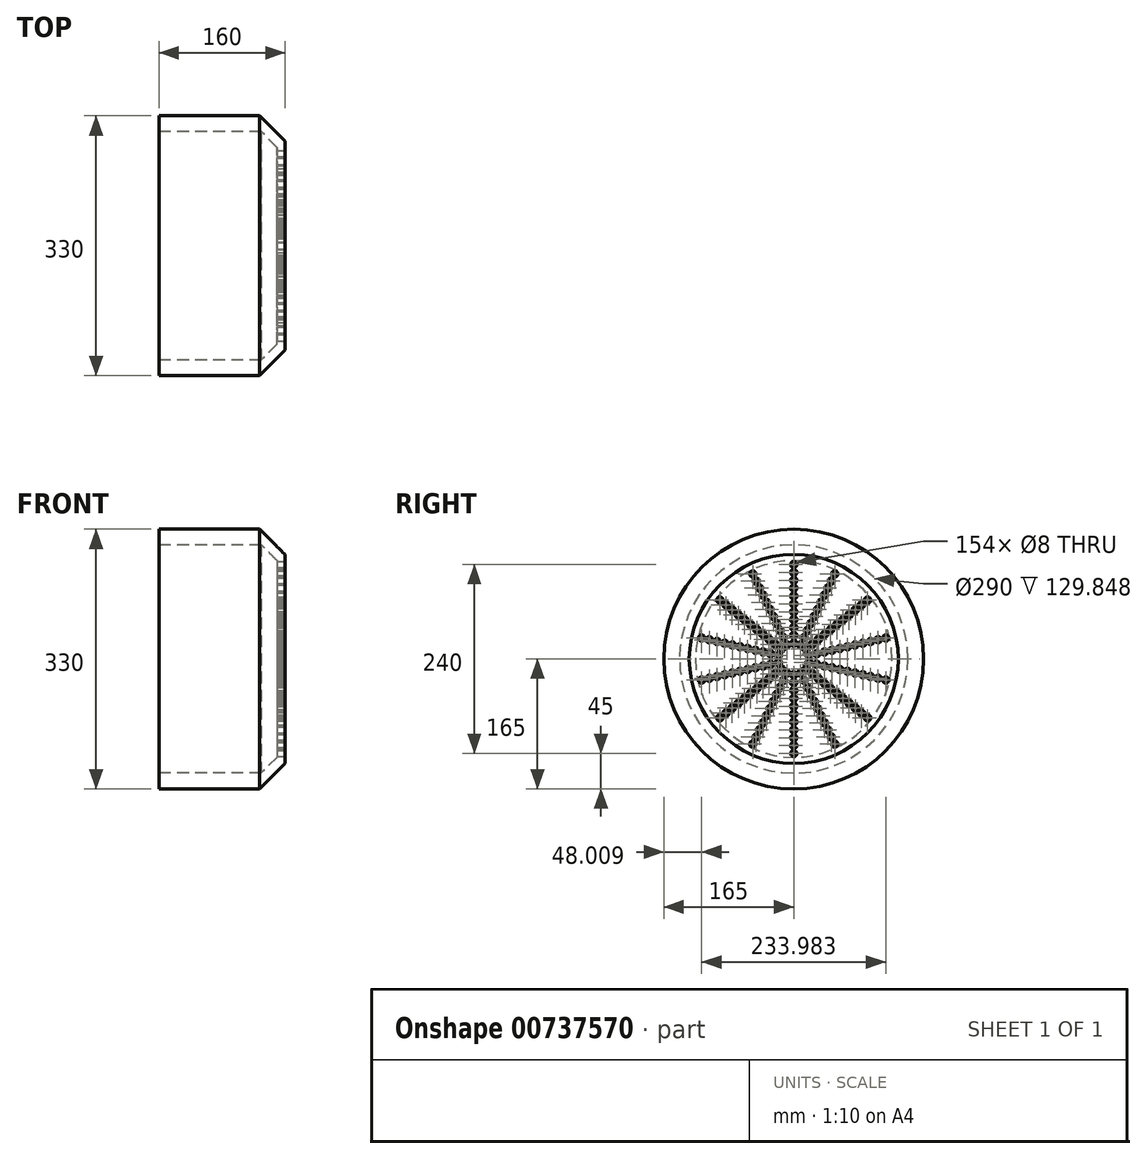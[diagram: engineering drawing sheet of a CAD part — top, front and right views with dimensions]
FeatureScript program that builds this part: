
annotation { "Feature Type Name" : "Feature", "Feature Type Description" : "" }
export const myFeature = defineFeature(function(context is Context, id is Id, definition is map)
    precondition{}
    {
        {
            var Q0;
            Q0=qCreatedBy(makeId("Front.planeOp"),FACE);
            var sketch = newSketch(context, id + "F0", { "sketchPlane" : qUnion([Q0])});
            skLineSegment(sketch, "E0.bottom", {"start": v(170, 0) * mm, "end": v(180, 0) * mm});
            skLineSegment(sketch, "E0.top", {"start": v(20, 165) * mm, "end": v(147.78, 165) * mm});
            skLineSegment(sketch, "E0.left", {"start": v(20, 145) * mm, "end": v(20, 165) * mm});
            skLineSegment(sketch, "E0.right", {"start": v(180, 0) * mm, "end": v(180, 132.78) * mm});
            skLineSegment(sketch, "E1", {"start": v(20, 145) * mm, "end": v(125.56, 145) * mm});
            skLineSegment(sketch, "E2", {"start": v(170, 100.56) * mm, "end": v(170, 0) * mm});
            skLineSegment(sketch, "E3", {"start": v(147.78, 165) * mm, "end": v(180, 132.78) * mm});
            skPoint(sketch, "E3.startSnap0", {"position": v(147.78, 122.78) * mm});
            skLineSegment(sketch, "E4", {"start": v(170, 100.56) * mm, "end": v(170, 124.85) * mm});
            skLineSegment(sketch, "E5", {"start": v(170, 124.85) * mm, "end": v(149.85, 145) * mm});
            skLineSegment(sketch, "E6", {"start": v(125.56, 145) * mm, "end": v(149.85, 145) * mm});
            skSolve(sketch);
        }
        {
            var Q0;
            Q0 = qSketchRegion(id + "F0", true);
            var Q1;
            Q1=sQuery(id+"F0.wireOp",EDGE,"E0.bottom");
            revolve(context, id + "F1", {"surfaceOperationType" : NewSurfaceOperationType.NEW, "entities" : qUnion([Q0]), "axis" : qUnion([Q1]), "revolveType" : RevolveType.FULL});
        }
        {
            var Q0;
            Q0=makeQuery(id+"F1.opRevolve","SWEPT_FACE",FACE,{"disambiguationData":[OSD([sQuery(id+"F0.wireOp",EDGE,"E0.right")])]});
            var sketch = newSketch(context, id + "F2", { "sketchPlane" : qUnion([Q0])});
            skCircle(sketch, "E7", {"center": v(0, 20) * mm, "radius": 4 * mm});
            skCircle(sketch, "E8.0.1.0", {"center": v(0, 30) * mm, "radius": 4 * mm});
            skCircle(sketch, "E8.0.2.0", {"center": v(0, 40) * mm, "radius": 4 * mm});
            skCircle(sketch, "E8.0.3.0", {"center": v(0, 50) * mm, "radius": 4 * mm});
            skCircle(sketch, "E8.0.4.0", {"center": v(0, 60) * mm, "radius": 4 * mm});
            skCircle(sketch, "E8.0.5.0", {"center": v(0, 70) * mm, "radius": 4 * mm});
            skCircle(sketch, "E8.0.6.0", {"center": v(0, 80) * mm, "radius": 4 * mm});
            skCircle(sketch, "E8.0.7.0", {"center": v(0, 90) * mm, "radius": 4 * mm});
            skCircle(sketch, "E8.0.8.0", {"center": v(0, 100) * mm, "radius": 4 * mm});
            skCircle(sketch, "E8.0.9.0", {"center": v(0, 110) * mm, "radius": 4 * mm});
            skCircle(sketch, "E8.0.10.0", {"center": v(0, 120) * mm, "radius": 4 * mm});
            skLineSegment(sketch, "E8.direction1", {"start": v(0, 20) * mm, "end": v(25, 20) * mm, "construction": true});
            skLineSegment(sketch, "E8.direction2", {"start": v(0, 20) * mm, "end": v(0, 30) * mm, "construction": true});
            skCircle(sketch, "E9.1.0", {"center": v(-21.7, 45.05) * mm, "radius": 4 * mm});
            skCircle(sketch, "E9.1.1", {"center": v(-13.02, 27.03) * mm, "radius": 4 * mm});
            skCircle(sketch, "E9.1.2", {"center": v(-43.39, 90.1) * mm, "radius": 4 * mm});
            skCircle(sketch, "E9.1.3", {"center": v(-39.05, 81.09) * mm, "radius": 4 * mm});
            skCircle(sketch, "E9.1.4", {"center": v(-26.03, 54.06) * mm, "radius": 4 * mm});
            skCircle(sketch, "E9.1.5", {"center": v(-30.37, 63.07) * mm, "radius": 4 * mm});
            skCircle(sketch, "E9.1.6", {"center": v(-34.71, 72.08) * mm, "radius": 4 * mm});
            skCircle(sketch, "E9.1.7", {"center": v(-8.68, 18.02) * mm, "radius": 4 * mm});
            skCircle(sketch, "E9.1.8", {"center": v(-17.36, 36.04) * mm, "radius": 4 * mm});
            skCircle(sketch, "E9.1.9", {"center": v(-52.07, 108.12) * mm, "radius": 4 * mm});
            skCircle(sketch, "E9.1.10", {"center": v(-47.73, 99.1) * mm, "radius": 4 * mm});
            skLineSegment(sketch, "E9.1.11", {"start": v(-8.68, 18.02) * mm, "end": v(-13.02, 27.03) * mm, "construction": true});
            skCircle(sketch, "E9.2.0", {"center": v(-39.1, 31.17) * mm, "radius": 4 * mm});
            skCircle(sketch, "E9.2.1", {"center": v(-23.45, 18.7) * mm, "radius": 4 * mm});
            skCircle(sketch, "E9.2.2", {"center": v(-78.18, 62.35) * mm, "radius": 4 * mm});
            skCircle(sketch, "E9.2.3", {"center": v(-70.36, 56.11) * mm, "radius": 4 * mm});
            skCircle(sketch, "E9.2.4", {"center": v(-46.9, 37.4) * mm, "radius": 4 * mm});
            skCircle(sketch, "E9.2.5", {"center": v(-54.73, 43.64) * mm, "radius": 4 * mm});
            skCircle(sketch, "E9.2.6", {"center": v(-62.55, 49.88) * mm, "radius": 4 * mm});
            skCircle(sketch, "E9.2.7", {"center": v(-15.64, 12.47) * mm, "radius": 4 * mm});
            skCircle(sketch, "E9.2.8", {"center": v(-31.27, 24.94) * mm, "radius": 4 * mm});
            skCircle(sketch, "E9.2.9", {"center": v(-93.82, 74.82) * mm, "radius": 4 * mm});
            skCircle(sketch, "E9.2.10", {"center": v(-86, 68.58) * mm, "radius": 4 * mm});
            skLineSegment(sketch, "E9.2.11", {"start": v(-15.64, 12.47) * mm, "end": v(-23.45, 18.7) * mm, "construction": true});
            skCircle(sketch, "E9.3.0", {"center": v(-48.75, 11.13) * mm, "radius": 4 * mm});
            skCircle(sketch, "E9.3.1", {"center": v(-29.25, 6.68) * mm, "radius": 4 * mm});
            skCircle(sketch, "E9.3.2", {"center": v(-97.5, 22.25) * mm, "radius": 4 * mm});
            skCircle(sketch, "E9.3.3", {"center": v(-87.74, 20.03) * mm, "radius": 4 * mm});
            skCircle(sketch, "E9.3.4", {"center": v(-58.5, 13.35) * mm, "radius": 4 * mm});
            skCircle(sketch, "E9.3.5", {"center": v(-68.24, 15.58) * mm, "radius": 4 * mm});
            skCircle(sketch, "E9.3.6", {"center": v(-78, 17.8) * mm, "radius": 4 * mm});
            skCircle(sketch, "E9.3.7", {"center": v(-19.5, 4.45) * mm, "radius": 4 * mm});
            skCircle(sketch, "E9.3.8", {"center": v(-39, 8.9) * mm, "radius": 4 * mm});
            skCircle(sketch, "E9.3.9", {"center": v(-117, 26.7) * mm, "radius": 4 * mm});
            skCircle(sketch, "E9.3.10", {"center": v(-107.24, 24.48) * mm, "radius": 4 * mm});
            skLineSegment(sketch, "E9.3.11", {"start": v(-19.5, 4.45) * mm, "end": v(-29.25, 6.68) * mm, "construction": true});
            skCircle(sketch, "E9.4.0", {"center": v(-48.75, -11.13) * mm, "radius": 4 * mm});
            skCircle(sketch, "E9.4.1", {"center": v(-29.25, -6.68) * mm, "radius": 4 * mm});
            skCircle(sketch, "E9.4.2", {"center": v(-97.5, -22.25) * mm, "radius": 4 * mm});
            skCircle(sketch, "E9.4.3", {"center": v(-87.74, -20.03) * mm, "radius": 4 * mm});
            skCircle(sketch, "E9.4.4", {"center": v(-58.5, -13.35) * mm, "radius": 4 * mm});
            skCircle(sketch, "E9.4.5", {"center": v(-68.24, -15.58) * mm, "radius": 4 * mm});
            skCircle(sketch, "E9.4.6", {"center": v(-78, -17.8) * mm, "radius": 4 * mm});
            skCircle(sketch, "E9.4.7", {"center": v(-19.5, -4.45) * mm, "radius": 4 * mm});
            skCircle(sketch, "E9.4.8", {"center": v(-39, -8.9) * mm, "radius": 4 * mm});
            skCircle(sketch, "E9.4.9", {"center": v(-117, -26.7) * mm, "radius": 4 * mm});
            skCircle(sketch, "E9.4.10", {"center": v(-107.24, -24.48) * mm, "radius": 4 * mm});
            skLineSegment(sketch, "E9.4.11", {"start": v(-19.5, -4.45) * mm, "end": v(-29.25, -6.68) * mm, "construction": true});
            skCircle(sketch, "E9.5.0", {"center": v(-39.1, -31.17) * mm, "radius": 4 * mm});
            skCircle(sketch, "E9.5.1", {"center": v(-23.45, -18.7) * mm, "radius": 4 * mm});
            skCircle(sketch, "E9.5.2", {"center": v(-78.18, -62.35) * mm, "radius": 4 * mm});
            skCircle(sketch, "E9.5.3", {"center": v(-70.36, -56.11) * mm, "radius": 4 * mm});
            skCircle(sketch, "E9.5.4", {"center": v(-46.9, -37.4) * mm, "radius": 4 * mm});
            skCircle(sketch, "E9.5.5", {"center": v(-54.73, -43.64) * mm, "radius": 4 * mm});
            skCircle(sketch, "E9.5.6", {"center": v(-62.55, -49.88) * mm, "radius": 4 * mm});
            skCircle(sketch, "E9.5.7", {"center": v(-15.64, -12.47) * mm, "radius": 4 * mm});
            skCircle(sketch, "E9.5.8", {"center": v(-31.27, -24.94) * mm, "radius": 4 * mm});
            skCircle(sketch, "E9.5.9", {"center": v(-93.82, -74.82) * mm, "radius": 4 * mm});
            skCircle(sketch, "E9.5.10", {"center": v(-86, -68.58) * mm, "radius": 4 * mm});
            skLineSegment(sketch, "E9.5.11", {"start": v(-15.64, -12.47) * mm, "end": v(-23.45, -18.7) * mm, "construction": true});
            skCircle(sketch, "E9.6.0", {"center": v(-21.7, -45.05) * mm, "radius": 4 * mm});
            skCircle(sketch, "E9.6.1", {"center": v(-13.02, -27.03) * mm, "radius": 4 * mm});
            skCircle(sketch, "E9.6.2", {"center": v(-43.39, -90.1) * mm, "radius": 4 * mm});
            skCircle(sketch, "E9.6.3", {"center": v(-39.05, -81.09) * mm, "radius": 4 * mm});
            skCircle(sketch, "E9.6.4", {"center": v(-26.03, -54.06) * mm, "radius": 4 * mm});
            skCircle(sketch, "E9.6.5", {"center": v(-30.37, -63.07) * mm, "radius": 4 * mm});
            skCircle(sketch, "E9.6.6", {"center": v(-34.71, -72.08) * mm, "radius": 4 * mm});
            skCircle(sketch, "E9.6.7", {"center": v(-8.68, -18.02) * mm, "radius": 4 * mm});
            skCircle(sketch, "E9.6.8", {"center": v(-17.36, -36.04) * mm, "radius": 4 * mm});
            skCircle(sketch, "E9.6.9", {"center": v(-52.07, -108.12) * mm, "radius": 4 * mm});
            skCircle(sketch, "E9.6.10", {"center": v(-47.73, -99.1) * mm, "radius": 4 * mm});
            skLineSegment(sketch, "E9.6.11", {"start": v(-8.68, -18.02) * mm, "end": v(-13.02, -27.03) * mm, "construction": true});
            skCircle(sketch, "E9.7.0", {"center": v(0, -50) * mm, "radius": 4 * mm});
            skCircle(sketch, "E9.7.1", {"center": v(0, -30) * mm, "radius": 4 * mm});
            skCircle(sketch, "E9.7.2", {"center": v(0, -100) * mm, "radius": 4 * mm});
            skCircle(sketch, "E9.7.3", {"center": v(0, -90) * mm, "radius": 4 * mm});
            skCircle(sketch, "E9.7.4", {"center": v(0, -60) * mm, "radius": 4 * mm});
            skCircle(sketch, "E9.7.5", {"center": v(0, -70) * mm, "radius": 4 * mm});
            skCircle(sketch, "E9.7.6", {"center": v(0, -80) * mm, "radius": 4 * mm});
            skCircle(sketch, "E9.7.7", {"center": v(0, -20) * mm, "radius": 4 * mm});
            skCircle(sketch, "E9.7.8", {"center": v(0, -40) * mm, "radius": 4 * mm});
            skCircle(sketch, "E9.7.9", {"center": v(0, -120) * mm, "radius": 4 * mm});
            skCircle(sketch, "E9.7.10", {"center": v(0, -110) * mm, "radius": 4 * mm});
            skLineSegment(sketch, "E9.7.11", {"start": v(0, -20) * mm, "end": v(0, -30) * mm, "construction": true});
            skCircle(sketch, "E9.8.0", {"center": v(21.7, -45.05) * mm, "radius": 4 * mm});
            skCircle(sketch, "E9.8.1", {"center": v(13.02, -27.03) * mm, "radius": 4 * mm});
            skCircle(sketch, "E9.8.2", {"center": v(43.39, -90.1) * mm, "radius": 4 * mm});
            skCircle(sketch, "E9.8.3", {"center": v(39.05, -81.09) * mm, "radius": 4 * mm});
            skCircle(sketch, "E9.8.4", {"center": v(26.03, -54.06) * mm, "radius": 4 * mm});
            skCircle(sketch, "E9.8.5", {"center": v(30.37, -63.07) * mm, "radius": 4 * mm});
            skCircle(sketch, "E9.8.6", {"center": v(34.71, -72.08) * mm, "radius": 4 * mm});
            skCircle(sketch, "E9.8.7", {"center": v(8.68, -18.02) * mm, "radius": 4 * mm});
            skCircle(sketch, "E9.8.8", {"center": v(17.36, -36.04) * mm, "radius": 4 * mm});
            skCircle(sketch, "E9.8.9", {"center": v(52.07, -108.12) * mm, "radius": 4 * mm});
            skCircle(sketch, "E9.8.10", {"center": v(47.73, -99.1) * mm, "radius": 4 * mm});
            skLineSegment(sketch, "E9.8.11", {"start": v(8.68, -18.02) * mm, "end": v(13.02, -27.03) * mm, "construction": true});
            skCircle(sketch, "E9.9.0", {"center": v(39.1, -31.17) * mm, "radius": 4 * mm});
            skCircle(sketch, "E9.9.1", {"center": v(23.45, -18.7) * mm, "radius": 4 * mm});
            skCircle(sketch, "E9.9.2", {"center": v(78.18, -62.35) * mm, "radius": 4 * mm});
            skCircle(sketch, "E9.9.3", {"center": v(70.36, -56.11) * mm, "radius": 4 * mm});
            skCircle(sketch, "E9.9.4", {"center": v(46.9, -37.4) * mm, "radius": 4 * mm});
            skCircle(sketch, "E9.9.5", {"center": v(54.73, -43.64) * mm, "radius": 4 * mm});
            skCircle(sketch, "E9.9.6", {"center": v(62.55, -49.88) * mm, "radius": 4 * mm});
            skCircle(sketch, "E9.9.7", {"center": v(15.64, -12.47) * mm, "radius": 4 * mm});
            skCircle(sketch, "E9.9.8", {"center": v(31.27, -24.94) * mm, "radius": 4 * mm});
            skCircle(sketch, "E9.9.9", {"center": v(93.82, -74.82) * mm, "radius": 4 * mm});
            skCircle(sketch, "E9.9.10", {"center": v(86, -68.58) * mm, "radius": 4 * mm});
            skLineSegment(sketch, "E9.9.11", {"start": v(15.64, -12.47) * mm, "end": v(23.45, -18.7) * mm, "construction": true});
            skCircle(sketch, "E9.10.0", {"center": v(48.75, -11.13) * mm, "radius": 4 * mm});
            skCircle(sketch, "E9.10.1", {"center": v(29.25, -6.68) * mm, "radius": 4 * mm});
            skCircle(sketch, "E9.10.2", {"center": v(97.5, -22.25) * mm, "radius": 4 * mm});
            skCircle(sketch, "E9.10.3", {"center": v(87.74, -20.03) * mm, "radius": 4 * mm});
            skCircle(sketch, "E9.10.4", {"center": v(58.5, -13.35) * mm, "radius": 4 * mm});
            skCircle(sketch, "E9.10.5", {"center": v(68.24, -15.58) * mm, "radius": 4 * mm});
            skCircle(sketch, "E9.10.6", {"center": v(78, -17.8) * mm, "radius": 4 * mm});
            skCircle(sketch, "E9.10.7", {"center": v(19.5, -4.45) * mm, "radius": 4 * mm});
            skCircle(sketch, "E9.10.8", {"center": v(39, -8.9) * mm, "radius": 4 * mm});
            skCircle(sketch, "E9.10.9", {"center": v(117, -26.7) * mm, "radius": 4 * mm});
            skCircle(sketch, "E9.10.10", {"center": v(107.24, -24.48) * mm, "radius": 4 * mm});
            skLineSegment(sketch, "E9.10.11", {"start": v(19.5, -4.45) * mm, "end": v(29.25, -6.68) * mm, "construction": true});
            skCircle(sketch, "E9.11.0", {"center": v(48.75, 11.13) * mm, "radius": 4 * mm});
            skCircle(sketch, "E9.11.1", {"center": v(29.25, 6.68) * mm, "radius": 4 * mm});
            skCircle(sketch, "E9.11.2", {"center": v(97.5, 22.25) * mm, "radius": 4 * mm});
            skCircle(sketch, "E9.11.3", {"center": v(87.74, 20.03) * mm, "radius": 4 * mm});
            skCircle(sketch, "E9.11.4", {"center": v(58.5, 13.35) * mm, "radius": 4 * mm});
            skCircle(sketch, "E9.11.5", {"center": v(68.24, 15.58) * mm, "radius": 4 * mm});
            skCircle(sketch, "E9.11.6", {"center": v(78, 17.8) * mm, "radius": 4 * mm});
            skCircle(sketch, "E9.11.7", {"center": v(19.5, 4.45) * mm, "radius": 4 * mm});
            skCircle(sketch, "E9.11.8", {"center": v(39, 8.9) * mm, "radius": 4 * mm});
            skCircle(sketch, "E9.11.9", {"center": v(117, 26.7) * mm, "radius": 4 * mm});
            skCircle(sketch, "E9.11.10", {"center": v(107.24, 24.48) * mm, "radius": 4 * mm});
            skLineSegment(sketch, "E9.11.11", {"start": v(19.5, 4.45) * mm, "end": v(29.25, 6.68) * mm, "construction": true});
            skCircle(sketch, "E9.12.0", {"center": v(39.1, 31.17) * mm, "radius": 4 * mm});
            skCircle(sketch, "E9.12.1", {"center": v(23.45, 18.7) * mm, "radius": 4 * mm});
            skCircle(sketch, "E9.12.2", {"center": v(78.18, 62.35) * mm, "radius": 4 * mm});
            skCircle(sketch, "E9.12.3", {"center": v(70.36, 56.11) * mm, "radius": 4 * mm});
            skCircle(sketch, "E9.12.4", {"center": v(46.9, 37.4) * mm, "radius": 4 * mm});
            skCircle(sketch, "E9.12.5", {"center": v(54.73, 43.64) * mm, "radius": 4 * mm});
            skCircle(sketch, "E9.12.6", {"center": v(62.55, 49.88) * mm, "radius": 4 * mm});
            skCircle(sketch, "E9.12.7", {"center": v(15.64, 12.47) * mm, "radius": 4 * mm});
            skCircle(sketch, "E9.12.8", {"center": v(31.27, 24.94) * mm, "radius": 4 * mm});
            skCircle(sketch, "E9.12.9", {"center": v(93.82, 74.82) * mm, "radius": 4 * mm});
            skCircle(sketch, "E9.12.10", {"center": v(86, 68.58) * mm, "radius": 4 * mm});
            skLineSegment(sketch, "E9.12.11", {"start": v(15.64, 12.47) * mm, "end": v(23.45, 18.7) * mm, "construction": true});
            skCircle(sketch, "E9.13.0", {"center": v(21.7, 45.05) * mm, "radius": 4 * mm});
            skCircle(sketch, "E9.13.1", {"center": v(13.02, 27.03) * mm, "radius": 4 * mm});
            skCircle(sketch, "E9.13.2", {"center": v(43.39, 90.1) * mm, "radius": 4 * mm});
            skCircle(sketch, "E9.13.3", {"center": v(39.05, 81.09) * mm, "radius": 4 * mm});
            skCircle(sketch, "E9.13.4", {"center": v(26.03, 54.06) * mm, "radius": 4 * mm});
            skCircle(sketch, "E9.13.5", {"center": v(30.37, 63.07) * mm, "radius": 4 * mm});
            skCircle(sketch, "E9.13.6", {"center": v(34.71, 72.08) * mm, "radius": 4 * mm});
            skCircle(sketch, "E9.13.7", {"center": v(8.68, 18.02) * mm, "radius": 4 * mm});
            skCircle(sketch, "E9.13.8", {"center": v(17.36, 36.04) * mm, "radius": 4 * mm});
            skCircle(sketch, "E9.13.9", {"center": v(52.07, 108.12) * mm, "radius": 4 * mm});
            skCircle(sketch, "E9.13.10", {"center": v(47.73, 99.1) * mm, "radius": 4 * mm});
            skLineSegment(sketch, "E9.13.11", {"start": v(8.68, 18.02) * mm, "end": v(13.02, 27.03) * mm, "construction": true});
            skPoint(sketch, "E9.center", {"position": v(0, 0) * mm});
            skSolve(sketch);
        }
        {
            var Q0;
            Q0 = qSketchRegion(id + "F2", true);
            extrude(context, id + "F3", {"entities" : qUnion([Q0]), "operationType" : NewBodyOperationType.REMOVE, "oppositeDirection" : true, "depth" : 25 * mm, "offsetDistance" : 25 * mm});
        }
    });
